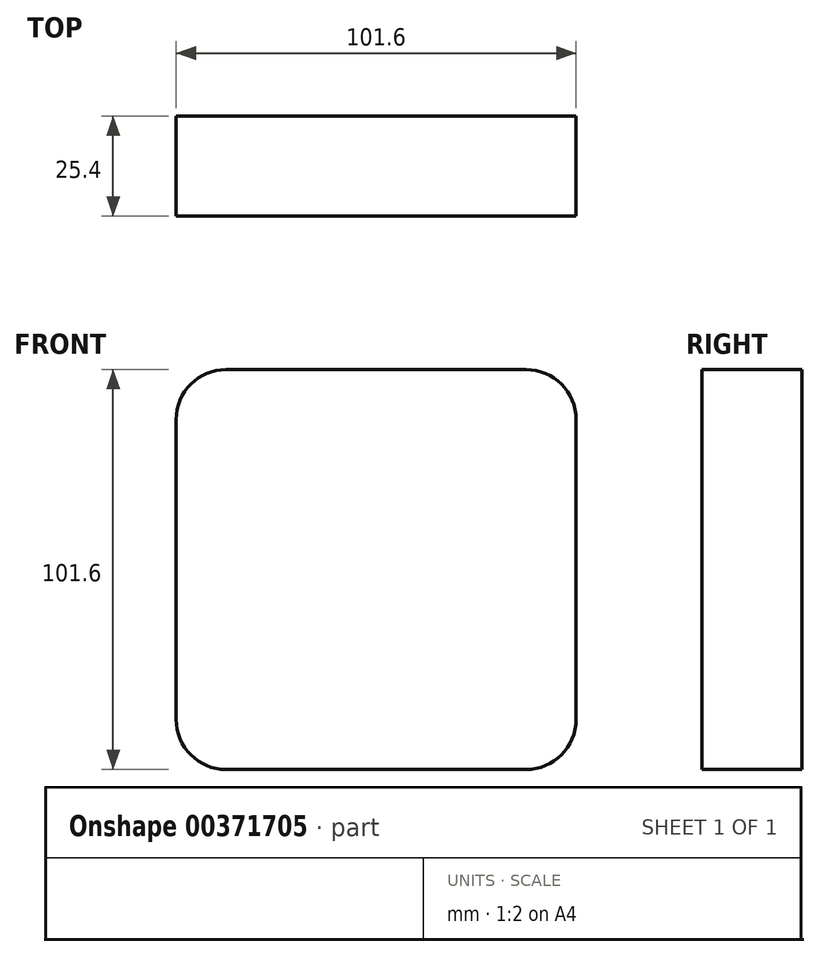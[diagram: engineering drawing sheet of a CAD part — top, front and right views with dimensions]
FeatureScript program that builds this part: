
annotation { "Feature Type Name" : "Feature", "Feature Type Description" : "" }
export const myFeature = defineFeature(function(context is Context, id is Id, definition is map)
    precondition{}
    {
        {
            var Q0;
            Q0=qCreatedBy(makeId("Front.planeOp"),FACE);
            var sketch = newSketch(context, id + "F0", { "sketchPlane" : qUnion([Q0])});
            skLineSegment(sketch, "E0.bottom", {"start": v(-52.85, 58.3) * mm, "end": v(48.75, 58.3) * mm});
            skLineSegment(sketch, "E0.top", {"start": v(-52.85, -43.3) * mm, "end": v(48.75, -43.3) * mm});
            skLineSegment(sketch, "E0.left", {"start": v(-52.85, 58.3) * mm, "end": v(-52.85, -43.3) * mm});
            skLineSegment(sketch, "E0.right", {"start": v(48.75, 58.3) * mm, "end": v(48.75, -43.3) * mm});
            skSolve(sketch);
        }
        {
            var Q0;
            Q0=makeQuery(id+"F0.imprint","IMPRINT",FACE,{"disambiguationData":[TD([[makeQuery(id+"F0.imprint","IMPRINT",EDGE,{"derivedFrom":sQuery(id+"F0.wireOp",EDGE,"E0.bottom")}),-1.0]])]});
            extrude(context, id + "F1", {"entities" : qUnion([Q0]), "depth" : 25.4 * mm});
        }
        {
            var Q0;
            Q0=makeQuery(id+"F1.opExtrude","SWEPT_EDGE",EDGE,{"disambiguationData":[OSD([sQuery(id+"F0.wireOp",EDGE,"E0.bottom"),sQuery(id+"F0.wireOp",EDGE,"E0.left")])]});
            var Q1;
            Q1=makeQuery(id+"F1.opExtrude","SWEPT_EDGE",EDGE,{"disambiguationData":[OSD([sQuery(id+"F0.wireOp",EDGE,"E0.bottom"),sQuery(id+"F0.wireOp",EDGE,"E0.right")])]});
            var Q2;
            Q2=makeQuery(id+"F1.opExtrude","SWEPT_EDGE",EDGE,{"disambiguationData":[OSD([sQuery(id+"F0.wireOp",EDGE,"E0.top"),sQuery(id+"F0.wireOp",EDGE,"E0.left")])]});
            var Q3;
            Q3=makeQuery(id+"F1.opExtrude","SWEPT_EDGE",EDGE,{"disambiguationData":[OSD([sQuery(id+"F0.wireOp",EDGE,"E0.top"),sQuery(id+"F0.wireOp",EDGE,"E0.right")])]});
            fillet(context, id + "F2", {"entities" : qUnion([Q0, Q1, Q2, Q3]), "radius" : 12.7 * mm, "tangentPropagation" : true, "allowEdgeOverflow" : false});
        }
    });
